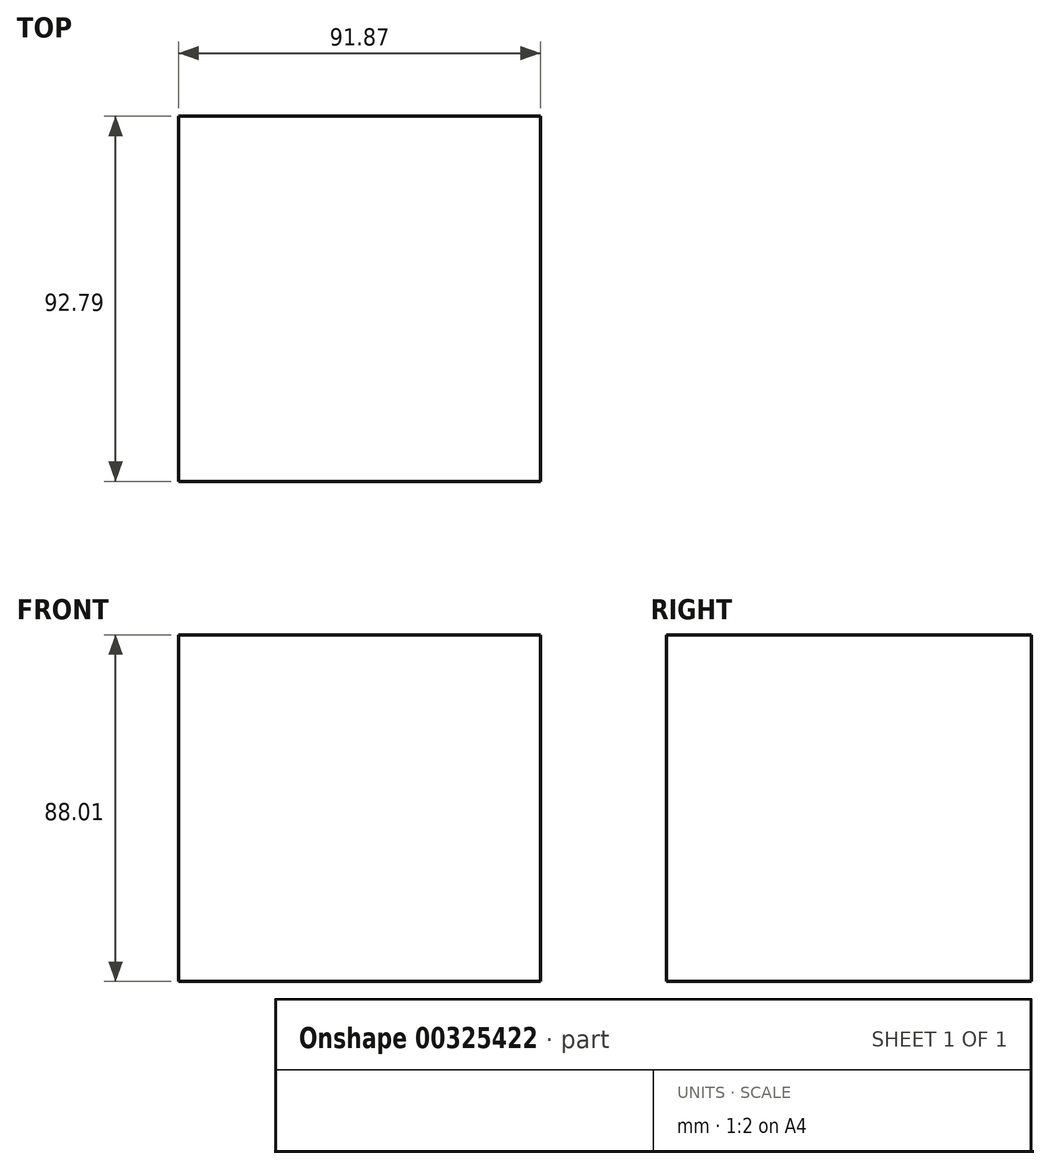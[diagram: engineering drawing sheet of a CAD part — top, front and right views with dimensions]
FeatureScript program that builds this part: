
annotation { "Feature Type Name" : "Feature", "Feature Type Description" : "" }
export const myFeature = defineFeature(function(context is Context, id is Id, definition is map)
    precondition{}
    {
        {
            var Q0;
            Q0=qCreatedBy(makeId("Top.planeOp"),FACE);
            var sketch = newSketch(context, id + "F0", { "sketchPlane" : qUnion([Q0])});
            skLineSegment(sketch, "E0.bottom", {"start": v(0, 0) * mm, "end": v(91.87, 0) * mm});
            skLineSegment(sketch, "E0.top", {"start": v(0, -92.79) * mm, "end": v(91.87, -92.79) * mm});
            skLineSegment(sketch, "E0.left", {"start": v(0, 0) * mm, "end": v(0, -92.79) * mm});
            skLineSegment(sketch, "E0.right", {"start": v(91.87, 0) * mm, "end": v(91.87, -92.79) * mm});
            skSolve(sketch);
        }
        {
            var Q0;
            Q0=makeQuery(id+"F0.imprint","IMPRINT",FACE,{"disambiguationData":[TD([[makeQuery(id+"F0.imprint","IMPRINT",EDGE,{"derivedFrom":sQuery(id+"F0.wireOp",EDGE,"E0.bottom")}),-1.0]])]});
            extrude(context, id + "F1", {"entities" : qUnion([Q0]), "depth" : 88 * mm});
        }
    });
